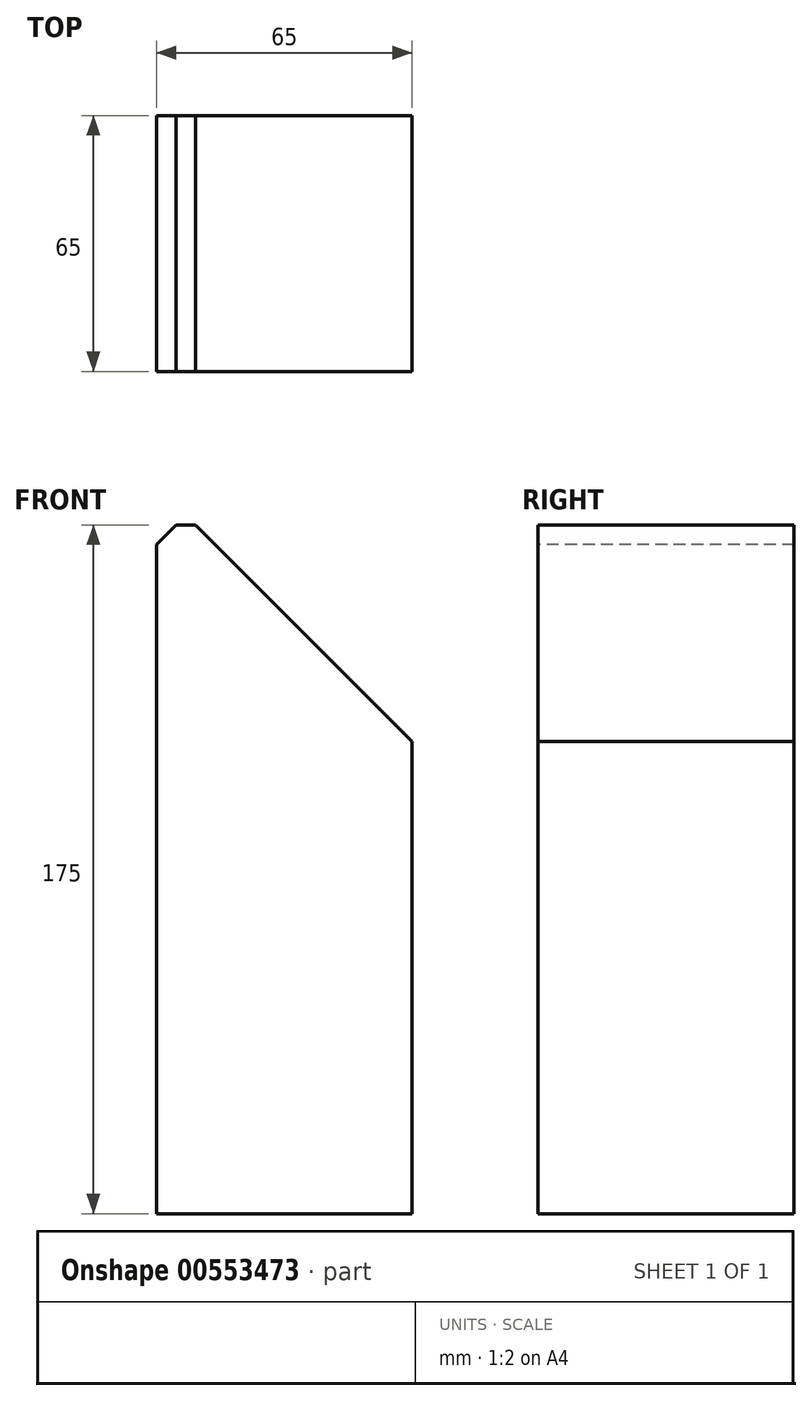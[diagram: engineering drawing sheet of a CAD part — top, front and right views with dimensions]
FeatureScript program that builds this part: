
annotation { "Feature Type Name" : "Feature", "Feature Type Description" : "" }
export const myFeature = defineFeature(function(context is Context, id is Id, definition is map)
    precondition{}
    {
        {
            var Q0;
            Q0=qCreatedBy(makeId("Top.planeOp"),FACE);
            var sketch = newSketch(context, id + "F0", { "sketchPlane" : qUnion([Q0])});
            skLineSegment(sketch, "E0.bottom", {"start": v(-32.5, 32.5) * mm, "end": v(32.5, 32.5) * mm});
            skLineSegment(sketch, "E0.top", {"start": v(-32.5, -32.5) * mm, "end": v(32.5, -32.5) * mm});
            skLineSegment(sketch, "E0.left", {"start": v(-32.5, 32.5) * mm, "end": v(-32.5, -32.5) * mm});
            skLineSegment(sketch, "E0.right", {"start": v(32.5, 32.5) * mm, "end": v(32.5, -32.5) * mm});
            skPoint(sketch, "E0.middle", {"position": v(0, 0) * mm});
            skSolve(sketch);
        }
        {
            var Q0;
            Q0=makeQuery(id+"F0.imprint","IMPRINT",FACE,{"disambiguationData":[TD([[makeQuery(id+"F0.imprint","IMPRINT",EDGE,{"derivedFrom":sQuery(id+"F0.wireOp",EDGE,"E0.bottom")}),-1.0]])]});
            extrude(context, id + "F1", {"entities" : qUnion([Q0]), "depth" : 350 * mm, "offsetDistance" : 25 * mm});
        }
        {
            var Q0;
            Q0=makeQuery(id+"F1.opExtrude","SWEPT_FACE",FACE,{"disambiguationData":[OSD([sQuery(id+"F0.wireOp",EDGE,"E0.top")])]});
            var sketch = newSketch(context, id + "F2", { "sketchPlane" : qUnion([Q0])});
            skLineSegment(sketch, "E1", {"start": v(32.5, 175) * mm, "end": v(-32.5, 175) * mm, "construction": true});
            skLineSegment(sketch, "E2", {"start": v(32.5, 120) * mm, "end": v(-22.5, 175) * mm});
            skLineSegment(sketch, "E3", {"start": v(-22.5, 175) * mm, "end": v(32.5, 230) * mm});
            skLineSegment(sketch, "E4", {"start": v(32.5, 120) * mm, "end": v(32.5, 230) * mm});
            skLineSegment(sketch, "E5", {"start": v(-27.5, 175) * mm, "end": v(-32.5, 170) * mm});
            skLineSegment(sketch, "E6", {"start": v(-32.5, 170) * mm, "end": v(-32.5, 180) * mm});
            skLineSegment(sketch, "E7", {"start": v(-32.5, 180) * mm, "end": v(-27.5, 175) * mm});
            skSolve(sketch);
        }
        {
            var Q0;
            Q0=makeQuery(id+"F2.imprint","IMPRINT",FACE,{"disambiguationData":[TD([[makeQuery(id+"F2.imprint","IMPRINT",EDGE,{"derivedFrom":sQuery(id+"F2.wireOp",EDGE,"E2")}),-1.0]])]});
            var Q1;
            Q1=makeQuery(id+"F2.imprint","IMPRINT",FACE,{"disambiguationData":[TD([[makeQuery(id+"F2.imprint","IMPRINT",EDGE,{"derivedFrom":sQuery(id+"F2.wireOp",EDGE,"E5")}),-1.0]])]});
            extrude(context, id + "F3", {"entities" : qUnion([Q0, Q1]), "operationType" : NewBodyOperationType.REMOVE, "endBound" : BoundingType.THROUGH_ALL, "oppositeDirection" : true, "depth" : 25 * mm, "offsetDistance" : 25 * mm});
        }
        {
            var Q0;
            Q0=makeQuery(id+"F3.boolean.opBoolean","COPY",FACE,{"derivedFrom":makeQuery(id+"F3.opExtrude","SWEPT_FACE",FACE,{"disambiguationData":[OSD([sQuery(id+"F2.wireOp",EDGE,"E2")])]})});
            var sketch = newSketch(context, id + "F4", { "sketchPlane" : qUnion([Q0])});
            skLineSegment(sketch, "E8.bottom", {"start": v(-61.87, -32.5) * mm, "end": v(-136.87, -32.5) * mm});
            skLineSegment(sketch, "E8.top", {"start": v(-61.87, 32.5) * mm, "end": v(-136.87, 32.5) * mm});
            skLineSegment(sketch, "E8.left", {"start": v(-61.87, -32.5) * mm, "end": v(-61.87, 32.5) * mm});
            skLineSegment(sketch, "E8.right", {"start": v(-136.87, -32.5) * mm, "end": v(-136.87, 32.5) * mm});
            skSolve(sketch);
        }
        {
            var Q0;
            Q0=makeQuery(id+"F4.imprint","IMPRINT",FACE,{"disambiguationData":[TD([[makeQuery(id+"F4.imprint","IMPRINT",EDGE,{"derivedFrom":sQuery(id+"F4.wireOp",EDGE,"E8.bottom")}),-1.0]])]});
            extrude(context, id + "F5", {"entities" : qUnion([Q0]), "depth" : 2 * mm, "offsetDistance" : 25 * mm});
        }
        {
            var Q0;
            Q0=makeQuery(id+"F3.boolean.opBoolean","COPY",FACE,{"derivedFrom":makeQuery(id+"F3.opExtrude","SWEPT_FACE",FACE,{"disambiguationData":[OSD([sQuery(id+"F2.wireOp",EDGE,"E3")])]})});
            var sketch = newSketch(context, id + "F6", { "sketchPlane" : qUnion([Q0])});
            skLineSegment(sketch, "E9.bottom", {"start": v(-32.5, 185.62) * mm, "end": v(32.5, 185.62) * mm});
            skLineSegment(sketch, "E9.top", {"start": v(-32.5, 110.62) * mm, "end": v(32.5, 110.62) * mm});
            skLineSegment(sketch, "E9.left", {"start": v(-32.5, 185.62) * mm, "end": v(-32.5, 110.62) * mm});
            skLineSegment(sketch, "E9.right", {"start": v(32.5, 185.62) * mm, "end": v(32.5, 110.62) * mm});
            skSolve(sketch);
        }
        {
            var Q0;
            Q0=makeQuery(id+"F6.imprint","IMPRINT",FACE,{"disambiguationData":[TD([[makeQuery(id+"F6.imprint","IMPRINT",EDGE,{"derivedFrom":sQuery(id+"F6.wireOp",EDGE,"E9.bottom")}),1.0]])]});
            extrude(context, id + "F7", {"entities" : qUnion([Q0]), "depth" : 2 * mm, "offsetDistance" : 25 * mm});
        }
        {
            var Q0;
            Q0=makeQuery(id+"F5.opExtrude","SWEPT_BODY",BODY,{"disambiguationData":[OSD([sQuery(id+"F4.wireOp",EDGE,"E8.bottom"),sQuery(id+"F4.wireOp",EDGE,"E8.top"),sQuery(id+"F4.wireOp",EDGE,"E8.left"),sQuery(id+"F4.wireOp",EDGE,"E8.right")])]});
            var Q1;
            Q1=makeQuery(id+"F7.opExtrude","SWEPT_BODY",BODY,{"disambiguationData":[OSD([sQuery(id+"F6.wireOp",EDGE,"E9.bottom"),sQuery(id+"F6.wireOp",EDGE,"E9.top"),sQuery(id+"F6.wireOp",EDGE,"E9.left"),sQuery(id+"F6.wireOp",EDGE,"E9.right")])]});
            deleteBodies(context, id + "F8", {"entities" : qUnion([Q0, Q1])});
        }
        {
            var Q0;
            Q0=makeQuery(id+"F1.opExtrude","SWEPT_FACE",FACE,{"disambiguationData":[OSD([sQuery(id+"F0.wireOp",EDGE,"E0.top")])]});
            var sketch = newSketch(context, id + "F9", { "sketchPlane" : qUnion([Q0])});
            skLineSegment(sketch, "E10", {"start": v(-27.5, 175) * mm, "end": v(-22.5, 175) * mm});
            skSolve(sketch);
        }
        {
            var Q0;
            Q0=makeQuery(id+"F9.imprint","IMPRINT",FACE,{"disambiguationData":[TD([[makeQuery(id+"F9.imprint","IMPRINT",EDGE,{"derivedFrom":sQuery(id+"F9.wireOp",EDGE,"E10")}),1.0]])]});
            extrude(context, id + "F10", {"entities" : qUnion([Q0]), "operationType" : NewBodyOperationType.REMOVE, "endBound" : BoundingType.THROUGH_ALL, "oppositeDirection" : true, "depth" : 25 * mm, "offsetDistance" : 25 * mm});
        }
    });
